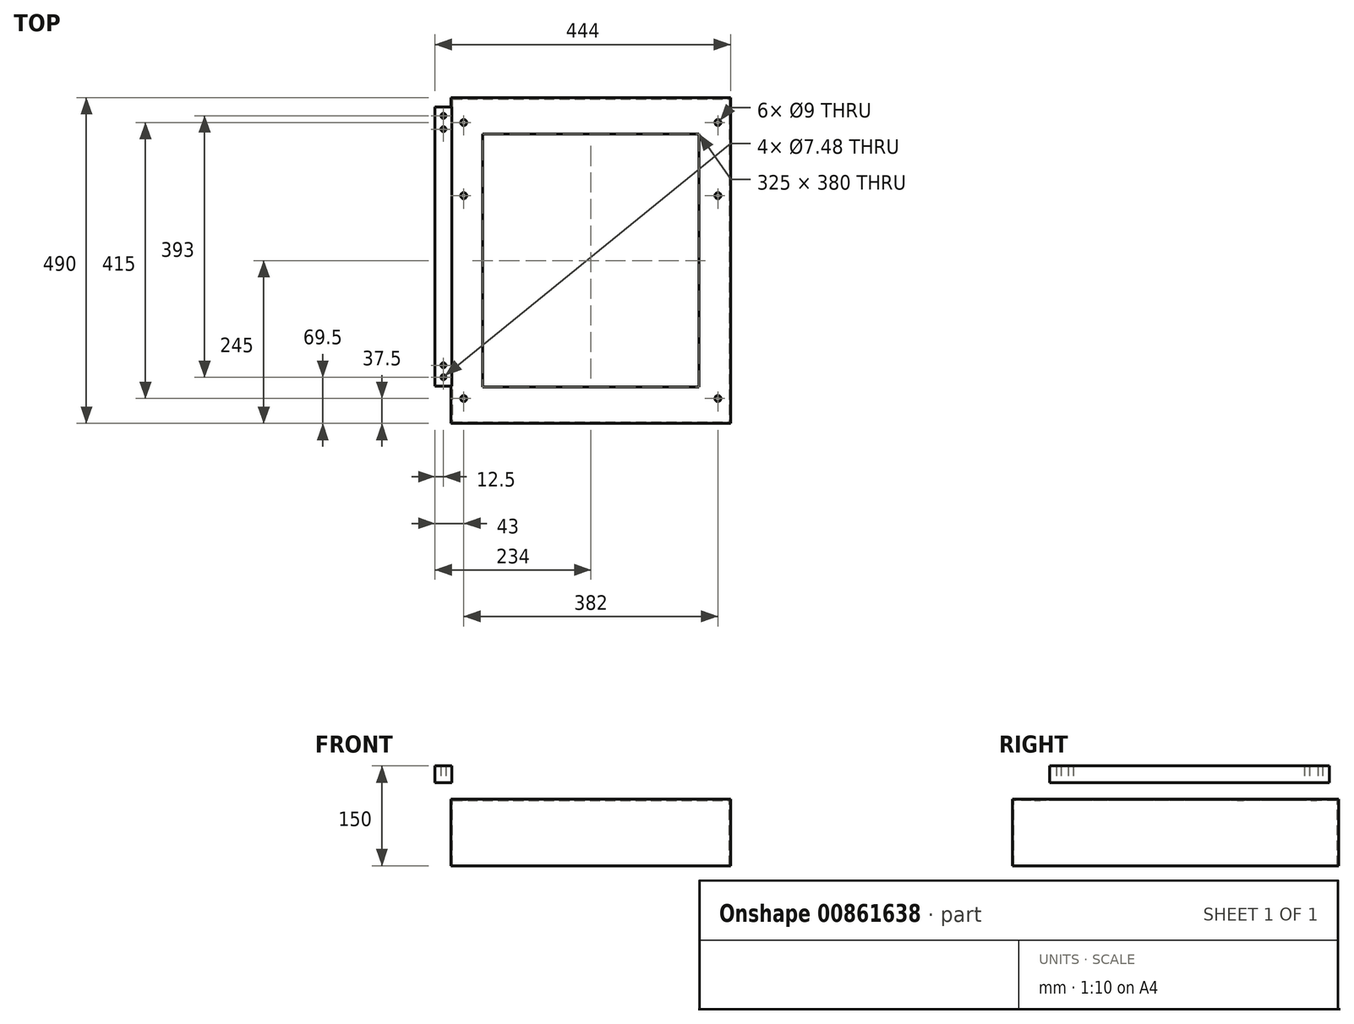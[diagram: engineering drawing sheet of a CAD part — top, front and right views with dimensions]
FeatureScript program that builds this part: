
annotation { "Feature Type Name" : "Feature", "Feature Type Description" : "" }
export const myFeature = defineFeature(function(context is Context, id is Id, definition is map)
    precondition{}
    {
        {
            var Q0;
            Q0=qCreatedBy(makeId("Top.planeOp"),FACE);
            var sketch = newSketch(context, id + "F0", { "sketchPlane" : qUnion([Q0])});
            skLineSegment(sketch, "E0.bottom", {"start": v(-210, 245) * mm, "end": v(210, 245) * mm});
            skLineSegment(sketch, "E0.top", {"start": v(-210, -245) * mm, "end": v(210, -245) * mm});
            skLineSegment(sketch, "E0.left", {"start": v(-210, 245) * mm, "end": v(-210, -245) * mm});
            skLineSegment(sketch, "E0.right", {"start": v(210, 245) * mm, "end": v(210, -245) * mm});
            skPoint(sketch, "E0.middle", {"position": v(0, 0) * mm});
            skSolve(sketch);
        }
        {
            var Q0;
            Q0 = qSketchRegion(id + "F0", true);
            extrude(context, id + "F1", {"entities" : qUnion([Q0]), "oppositeDirection" : true, "depth" : 100 * mm, "offsetDistance" : 25 * mm});
        }
        {
            var Q0;
            Q0=makeQuery(id+"F1.opExtrude","CAP_FACE",FACE,{"disambiguationData":[OSD([sQuery(id+"F0.wireOp",EDGE,"E0.bottom"),sQuery(id+"F0.wireOp",EDGE,"E0.top"),sQuery(id+"F0.wireOp",EDGE,"E0.left"),sQuery(id+"F0.wireOp",EDGE,"E0.right")])],"isStart":false});
            shell(context, id + "F2", {"entities" : qUnion([Q0]), "thickness" : 2 * mm});
        }
        {
            var Q0;
            Q0=makeQuery(id+"F1.opExtrude","CAP_FACE",FACE,{"disambiguationData":[OSD([sQuery(id+"F0.wireOp",EDGE,"E0.bottom"),sQuery(id+"F0.wireOp",EDGE,"E0.top"),sQuery(id+"F0.wireOp",EDGE,"E0.left"),sQuery(id+"F0.wireOp",EDGE,"E0.right")])],"isStart":true});
            var sketch = newSketch(context, id + "F3", { "sketchPlane" : qUnion([Q0])});
            skLineSegment(sketch, "E1.bottom", {"start": v(-162.5, 190) * mm, "end": v(162.5, 190) * mm});
            skLineSegment(sketch, "E1.top", {"start": v(-162.5, -190) * mm, "end": v(162.5, -190) * mm});
            skLineSegment(sketch, "E1.left", {"start": v(-162.5, 190) * mm, "end": v(-162.5, -190) * mm});
            skLineSegment(sketch, "E1.right", {"start": v(162.5, 190) * mm, "end": v(162.5, -190) * mm});
            skPoint(sketch, "E1.middle", {"position": v(0, 0) * mm});
            skSolve(sketch);
        }
        {
            var Q0;
            Q0 = qSketchRegion(id + "F3", true);
            extrude(context, id + "F4", {"entities" : qUnion([Q0]), "operationType" : NewBodyOperationType.REMOVE, "oppositeDirection" : true, "depth" : 25 * mm, "offsetDistance" : 25 * mm});
        }
        {
            var Q0;
            Q0=qCreatedBy(makeId("Top.planeOp"),FACE);
            var sketch = newSketch(context, id + "F5", { "sketchPlane" : qUnion([Q0])});
            skLineSegment(sketch, "E2", {"start": v(-191, 207.5) * mm, "end": v(-191, -207.5) * mm, "construction": true});
            skCircle(sketch, "E3", {"center": v(-191, -207.5) * mm, "radius": 4.5 * mm});
            skCircle(sketch, "E4", {"center": v(-191, 97.5) * mm, "radius": 4.5 * mm});
            skCircle(sketch, "E5", {"center": v(-191, 207.5) * mm, "radius": 4.5 * mm});
            skLineSegment(sketch, "E6", {"start": v(-191, 0) * mm, "end": v(0, 0) * mm, "construction": true});
            skLineSegment(sketch, "E7", {"start": v(0, 0) * mm, "end": v(0, 167.18) * mm, "construction": true});
            skLineSegment(sketch, "E8.MirrorCS", {"start": v(191, 207.5) * mm, "end": v(191, -207.5) * mm, "construction": true});
            skCircle(sketch, "E9.MirrorC", {"center": v(191, 207.5) * mm, "radius": 4.5 * mm});
            skCircle(sketch, "E10.MirrorC", {"center": v(191, -207.5) * mm, "radius": 4.5 * mm});
            skCircle(sketch, "E11.MirrorC", {"center": v(191, 97.5) * mm, "radius": 4.5 * mm});
            skSolve(sketch);
        }
        {
            var Q0;
            Q0 = qSketchRegion(id + "F5", true);
            extrude(context, id + "F6", {"entities" : qUnion([Q0]), "operationType" : NewBodyOperationType.REMOVE, "oppositeDirection" : true, "depth" : 25 * mm, "offsetDistance" : 25 * mm});
        }
        {
            var Q0;
            Q0=qCreatedBy(makeId("Top.planeOp"),FACE);
            cPlane(context, id + "F7", {"entities" : qUnion([Q0]), "cplaneType" : CPlaneType.OFFSET, "offset" : 25 * mm, "width" : 150 * mm, "height" : 150 * mm});
        }
        {
            var Q0;
            Q0=qCreatedBy(id+"F7.planeOp",FACE);
            var sketch = newSketch(context, id + "F8", { "sketchPlane" : qUnion([Q0])});
            skLineSegment(sketch, "E12.bottom", {"start": v(-234, 231) * mm, "end": v(-209, 231) * mm});
            skLineSegment(sketch, "E12.top", {"start": v(-234, -189) * mm, "end": v(-209, -189) * mm});
            skLineSegment(sketch, "E12.left", {"start": v(-234, 231) * mm, "end": v(-234, -189) * mm});
            skLineSegment(sketch, "E12.right", {"start": v(-209, 231) * mm, "end": v(-209, -189) * mm});
            skPoint(sketch, "E12.middle", {"position": v(-221.5, 21) * mm});
            skSolve(sketch);
        }
        {
            var Q0;
            Q0 = qSketchRegion(id + "F8", true);
            extrude(context, id + "F9", {"entities" : qUnion([Q0]), "depth" : 25 * mm, "offsetDistance" : 25 * mm});
        }
        {
            var Q0;
            Q0=qCreatedBy(id+"F7.planeOp",FACE);
            var sketch = newSketch(context, id + "F10", { "sketchPlane" : qUnion([Q0])});
            skLineSegment(sketch, "E13", {"start": v(-221.5, 217.5) * mm, "end": v(-221.5, -175.5) * mm, "construction": true});
            skCircle(sketch, "E14", {"center": v(-221.5, 217.5) * mm, "radius": 3.74 * mm});
            skCircle(sketch, "E15", {"center": v(-221.5, 197.5) * mm, "radius": 3.74 * mm});
            skCircle(sketch, "E16", {"center": v(-221.5, -175.5) * mm, "radius": 3.74 * mm});
            skCircle(sketch, "E17", {"center": v(-221.5, -157.5) * mm, "radius": 3.74 * mm});
            skLineSegment(sketch, "E18", {"start": v(-221.5, 207.5) * mm, "end": v(-191, 207.5) * mm, "construction": true});
            skSolve(sketch);
        }
        {
            var Q0;
            Q0 = qSketchRegion(id + "F10", true);
            extrude(context, id + "F11", {"entities" : qUnion([Q0]), "operationType" : NewBodyOperationType.REMOVE, "depth" : 25 * mm, "offsetDistance" : 25 * mm});
        }
    });
